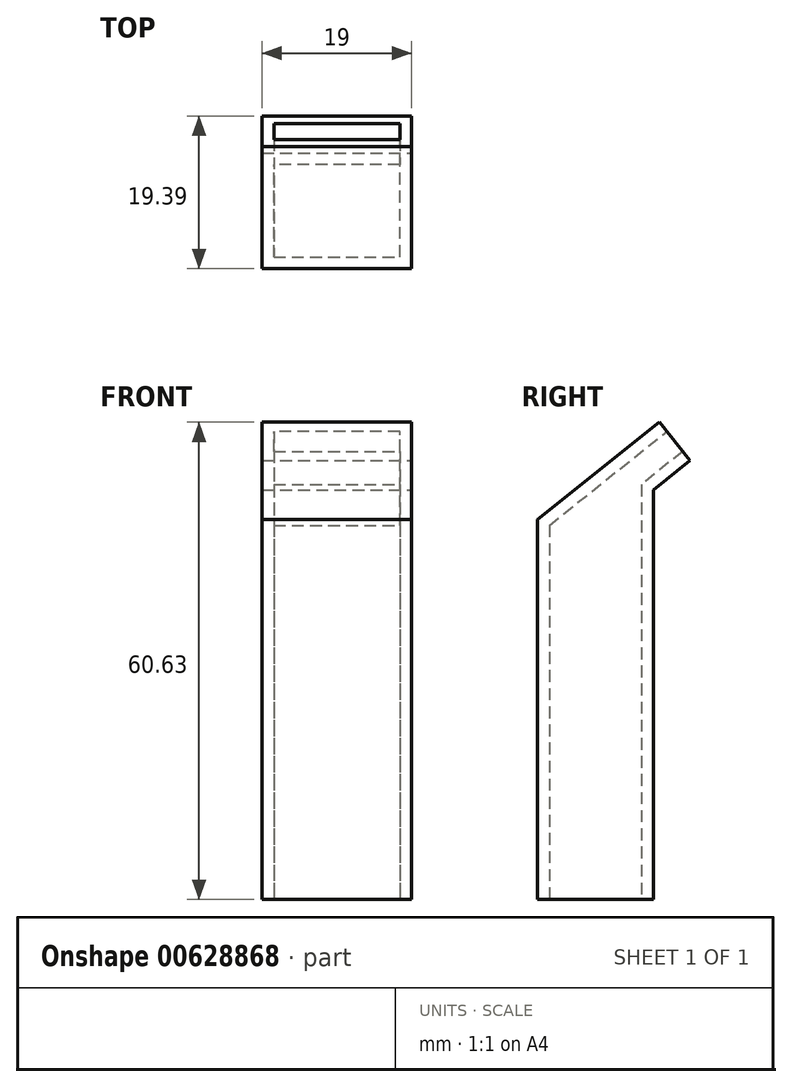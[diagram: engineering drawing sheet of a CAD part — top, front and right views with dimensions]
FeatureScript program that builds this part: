
annotation { "Feature Type Name" : "Feature", "Feature Type Description" : "" }
export const myFeature = defineFeature(function(context is Context, id is Id, definition is map)
    precondition{}
    {
        {
            var Q0;
            Q0=qCreatedBy(makeId("Top.planeOp"),FACE);
            var sketch = newSketch(context, id + "F0", { "sketchPlane" : qUnion([Q0])});
            skLineSegment(sketch, "E0.bottom", {"start": v(0, 0) * mm, "end": v(-17, 0) * mm});
            skLineSegment(sketch, "E0.top", {"start": v(0, 12.7) * mm, "end": v(-17, 12.7) * mm});
            skLineSegment(sketch, "E0.left", {"start": v(0, 0) * mm, "end": v(0, 12.7) * mm});
            skLineSegment(sketch, "E0.right", {"start": v(-17, 0) * mm, "end": v(-17, 12.7) * mm});
            skLineSegment(sketch, "E1.0", {"start": v(1, 13.7) * mm, "end": v(-18, 13.7) * mm});
            skLineSegment(sketch, "E1.1", {"start": v(1, -1) * mm, "end": v(1, 13.7) * mm});
            skLineSegment(sketch, "E1.2", {"start": v(1, -1) * mm, "end": v(-18, -1) * mm});
            skLineSegment(sketch, "E1.3", {"start": v(-18, -1) * mm, "end": v(-18, 13.7) * mm});
            skSolve(sketch);
        }
        {
            var Q0;
            Q0=makeQuery(id+"F0.imprint","IMPRINT",FACE,{"disambiguationData":[TD([[makeQuery(id+"F0.imprint","IMPRINT",EDGE,{"derivedFrom":sQuery(id+"F0.wireOp",EDGE,"E0.bottom")}),1.0]])]});
            var Q1;
            Q1=makeQuery(id+"F0.imprint","IMPRINT",FACE,{"disambiguationData":[TD([[makeQuery(id+"F0.imprint","IMPRINT",EDGE,{"derivedFrom":sQuery(id+"F0.wireOp",EDGE,"E0.bottom")}),-1.0]])]});
            extrude(context, id + "F1", {"entities" : qUnion([Q0, Q1]), "depth" : 40 * mm});
        }
        {
            var Q0;
            Q0=makeQuery(id+"F1.opExtrude","SWEPT_FACE",FACE,{"disambiguationData":[OSD([sQuery(id+"F0.wireOp",EDGE,"E1.1")])]});
            var sketch = newSketch(context, id + "F2", { "sketchPlane" : qUnion([Q0])});
            skLineSegment(sketch, "E2", {"start": v(-1, 28.25) * mm, "end": v(13.7, 40) * mm});
            skLineSegment(sketch, "E3", {"start": v(13.7, 40) * mm, "end": v(-1, 40) * mm});
            skLineSegment(sketch, "E4", {"start": v(-1, 40) * mm, "end": v(-1, 28.25) * mm});
            skSolve(sketch);
        }
        {
            var Q0;
            Q0=makeQuery(id+"F2.imprint","IMPRINT",FACE,{"disambiguationData":[TD([[makeQuery(id+"F2.imprint","IMPRINT",EDGE,{"derivedFrom":sQuery(id+"F2.wireOp",EDGE,"E2")}),1.0]])]});
            extrude(context, id + "F3", {"entities" : qUnion([Q0]), "operationType" : NewBodyOperationType.REMOVE, "endBound" : BoundingType.THROUGH_ALL, "oppositeDirection" : true, "depth" : 25 * mm});
        }
        {
            var Q0;
            Q0=makeQuery(id+"F1.opExtrude","SWEPT_FACE",FACE,{"disambiguationData":[OSD([sQuery(id+"F0.wireOp",EDGE,"E1.1")])]});
            var sketch = newSketch(context, id + "F4", { "sketchPlane" : qUnion([Q0])});
            skLineSegment(sketch, "E5", {"start": v(13.7, 40) * mm, "end": v(18.39, 43.75) * mm});
            skLineSegment(sketch, "E6", {"start": v(18.39, 43.75) * mm, "end": v(18.39, 35.75) * mm});
            skLineSegment(sketch, "E7", {"start": v(18.39, 35.75) * mm, "end": v(13.7, 32) * mm});
            skLineSegment(sketch, "E8", {"start": v(13.7, 40) * mm, "end": v(13.7, 32) * mm});
            skSolve(sketch);
        }
        {
            var Q0;
            Q0=makeQuery(id+"F4.imprint","IMPRINT",FACE,{"disambiguationData":[TD([[makeQuery(id+"F4.imprint","IMPRINT",EDGE,{"derivedFrom":sQuery(id+"F4.wireOp",EDGE,"E5")}),-1.0]])]});
            extrude(context, id + "F5", {"entities" : qUnion([Q0]), "operationType" : NewBodyOperationType.ADD, "oppositeDirection" : true, "depth" : 19 * mm});
        }
        {
            var Q0;
            Q0=makeQuery(id+"F5.opExtrude","SWEPT_FACE",FACE,{"disambiguationData":[OSD([sQuery(id+"F4.wireOp",EDGE,"E6")])]});
            var Q1;
            Q1=makeQuery(id+"F1.opExtrude","CAP_FACE",FACE,{"disambiguationData":[OSD([sQuery(id+"F0.wireOp",EDGE,"E1.0"),sQuery(id+"F0.wireOp",EDGE,"E1.1"),sQuery(id+"F0.wireOp",EDGE,"E1.2"),sQuery(id+"F0.wireOp",EDGE,"E1.3")])],"isStart":true});
            shell(context, id + "F6", {"entities" : qUnion([Q0, Q1]), "thickness" : 1.5 * mm});
        }
        {
            var Q0;
            Q0=makeQuery(id+"F5.boolean.opBoolean","MERGE",FACE,{"derivedFrom":[makeQuery(id+"F1.opExtrude","SWEPT_FACE",FACE,{"disambiguationData":[OSD([sQuery(id+"F0.wireOp",EDGE,"E1.3")])]}),makeQuery(id+"F5.opExtrude","CAP_FACE",FACE,{"disambiguationData":[OSD([sQuery(id+"F4.wireOp",EDGE,"E5"),sQuery(id+"F4.wireOp",EDGE,"E6"),sQuery(id+"F4.wireOp",EDGE,"E7"),sQuery(id+"F4.wireOp",EDGE,"E8")])],"isStart":false})]});
            var sketch = newSketch(context, id + "F7", { "sketchPlane" : qUnion([Q0])});
            skLineSegment(sketch, "E9", {"start": v(-18.39, 35.75) * mm, "end": v(-14.48, 40.63) * mm});
            skLineSegment(sketch, "E10", {"start": v(-14.48, 40.63) * mm, "end": v(-18.39, 43.75) * mm});
            skLineSegment(sketch, "E11", {"start": v(-18.39, 43.75) * mm, "end": v(-18.39, 35.75) * mm});
            skSolve(sketch);
        }
        {
            var Q0;
            Q0=makeQuery(id+"F7.imprint","IMPRINT",FACE,{"disambiguationData":[TD([[makeQuery(id+"F7.imprint","IMPRINT",EDGE,{"derivedFrom":sQuery(id+"F7.wireOp",EDGE,"E9")}),1.0]])]});
            extrude(context, id + "F8", {"entities" : qUnion([Q0]), "operationType" : NewBodyOperationType.REMOVE, "endBound" : BoundingType.THROUGH_ALL, "oppositeDirection" : true, "depth" : 25 * mm});
        }
        {
            var Q0;
            Q0=makeQuery(id+"F1.opExtrude","CAP_FACE",FACE,{"disambiguationData":[OSD([sQuery(id+"F0.wireOp",EDGE,"E1.0"),sQuery(id+"F0.wireOp",EDGE,"E1.1"),sQuery(id+"F0.wireOp",EDGE,"E1.2"),sQuery(id+"F0.wireOp",EDGE,"E1.3")])],"isStart":true});
            var sketch = newSketch(context, id + "F9", { "sketchPlane" : qUnion([Q0])});
            skSolve(sketch);
        }
        {
            var Q0;
            {var subQ3=sQuery(id+"F0.wireOp",EDGE,"E1.0");Q0=makeQuery(id+"F9.imprint","IMPRINT",FACE,{"disambiguationData":[TD([[makeQuery(id+"F9.imprint","IMPRINT",EDGE,{"derivedFrom":makeQuery(id+"F1.opExtrude","CAP_EDGE",EDGE,{"disambiguationData":[OSD([subQ3])],"isStart":true})}),-1.0]])]});}
            extrude(context, id + "F10", {"entities" : qUnion([Q0]), "operationType" : NewBodyOperationType.ADD, "depth" : 20 * mm});
        }
    });
